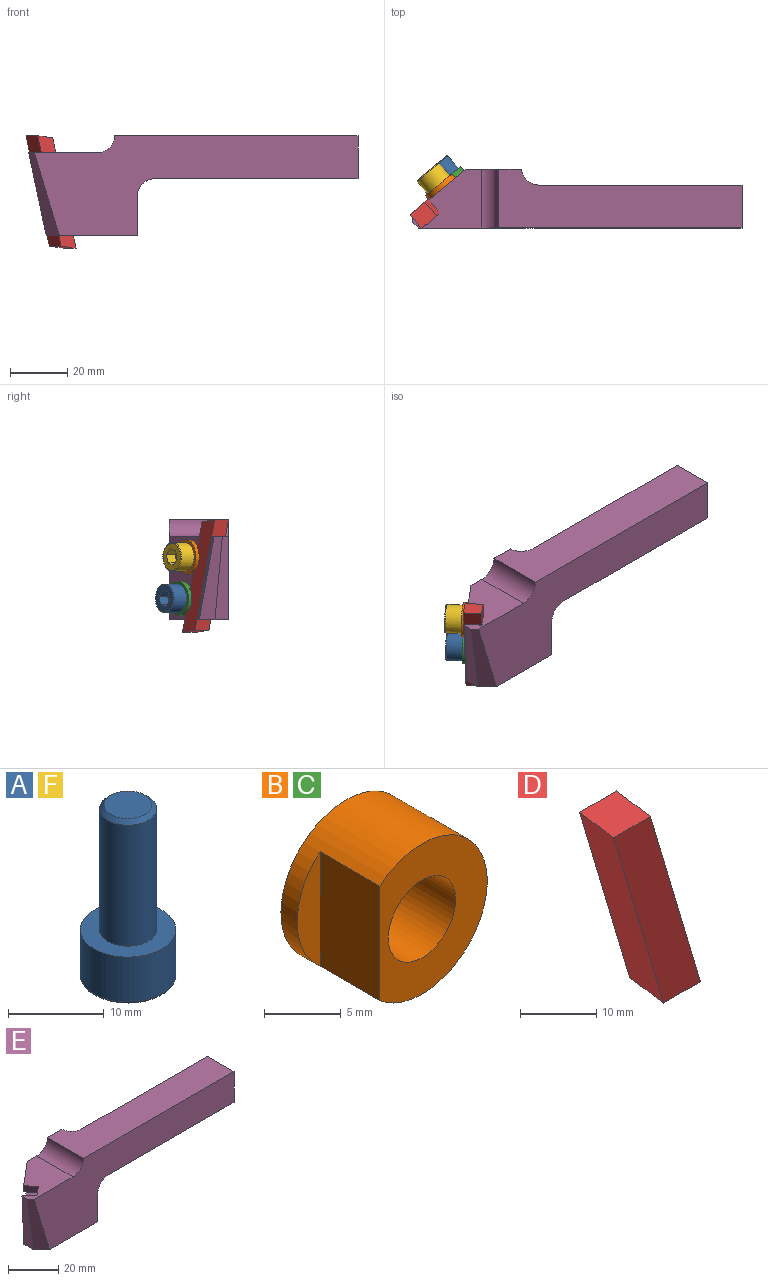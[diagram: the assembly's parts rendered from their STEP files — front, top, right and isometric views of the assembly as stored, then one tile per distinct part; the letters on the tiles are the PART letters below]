
ASSEMBLY  parts=6 mates=10
PART A: 14 faces, bbox 10.8x10.8x22 mm
  f0: plane 10x10mm, normal (0,0,1), area 50.3mm2, adj f1,f3
  f1: cylinder r=5mm len=10mm, axis (0,0,-1), area 180.6mm2, adj f0,f12
  f2: plane 9.5x9.5mm, normal (0,0,-1), area 47.5mm2, adj f5,f6,f7,f8,f9,f10,f12
  f3: cylinder r=3mm len=15.5mm, axis (0,0,-1), area 292.2mm2, adj f0,f13
  f4: plane 5x5mm, normal (0,0,1), area 19.6mm2, adj f13
  f5: plane 4x2.6mm, normal (0.87,-0.5,0), area 12mm2, adj f2,f6,f10,f11
  f6: plane 4x2.6mm, normal (0.87,0.5,0), area 12mm2, adj f2,f5,f7,f11
  f7: plane 4x3mm, normal (0,1,0), area 12mm2, adj f2,f6,f8,f11
  f8: plane 4x2.6mm, normal (-0.87,0.5,0), area 12mm2, adj f2,f7,f9,f11
  f9: plane 4x2.6mm, normal (-0.87,-0.5,0), area 12mm2, adj f2,f8,f10,f11
  f10: plane 4x3mm, normal (0,-1,0), area 12mm2, adj f2,f5,f9,f11
  f11: plane 6x5.2mm, normal (0,0,-1), area 23.4mm2, adj f5,f6,f7,f8,f9,f10
  f12: torus R=4.75mm, axis (0,0,1), area 12.1mm2, adj f1,f2
  f13: cone r=2.5mm half-angle=45deg, axis (0,0,-1), area 12.2mm2, adj f3,f4
PART B: 6 faces, bbox 12x7x12 mm
  f0: plane 12x9.9mm, normal (0,-1,0), area 69.6mm2, adj f1,f2,f4
  f1: cylinder r=3.1mm len=7mm, axis (0,1,0), area 136.3mm2, adj f0,f3
  f2: cylinder r=6mm len=12mm, axis (0,1,0), area 206.9mm2, adj f0,f3,f4,f5
  f3: plane 12x12mm, normal (0,1,0), area 82.9mm2, adj f1,f2
  f4: plane 9.12x5.5mm, normal (-1,0,0), area 50.2mm2, adj f0,f2,f5
  f5: plane 9.12x2.1mm, normal (0,-1,0), area 13.3mm2, adj f2,f4
PART C: same geometry as B
PART D: 6 faces, bbox 21.7x11.8x37.7 mm
  f0: plane 37.68x14.84mm, normal (0.93,-0.06,0.37), area 254mm2, adj f1,f3,f4,f5
  f1: plane 6.84x6.28mm, normal (0,-0.15,0.99), area 43.4mm2, adj f0,f2,f4,f5
  f2: plane 37.68x14.84mm, normal (-0.93,0.06,-0.37), area 254mm2, adj f1,f3,f4,f5
  f3: plane 6.84x6.28mm, normal (0,0.15,-0.99), area 43.4mm2, adj f0,f2,f4,f5
  f4: plane 36.73x21.68mm, normal (0,-0.99,-0.15), area 254mm2, adj f0,f1,f2,f3
  f5: plane 36.73x21.68mm, normal (0,0.99,0.15), area 254mm2, adj f0,f1,f2,f3
PART E: 27 faces, bbox 115x20.5x35 mm
  f0: plane 85x20.5mm, normal (0,0,1), area 1326.7mm2, adj f1,f3,f9,f11,f12,f25
  f1: cylinder r=6mm len=20.5mm, axis (0,0,1), area 151.5mm2, adj f0,f2,f11,f25
  f2: cylinder r=6mm len=20.5mm, axis (0,1,0), area 161.8mm2, adj f1,f9,f11,f24,f26
  f3: plane 15x15mm, normal (1,0,0), area 225mm2, adj f0,f9,f25,f26
  f4: plane 29x12.93mm, normal (-0.64,0.77,0), area 171.5mm2, adj f5,f6,f7,f8,f11,f16,f18,f21
  f5: plane 4.91x4.25mm, normal (-0.74,-0.62,-0.27), area 13.3mm2, adj f4,f8,f17,f21
  f6: plane 5.84x5.56mm, normal (-0.74,-0.62,-0.27), area 35.7mm2, adj f4,f17,f18,f21
  f7: plane 24x20.5mm, normal (0,0,1), area 305.4mm2, adj f4,f9,f10,f11,f12,f13,f14,f15
  f8: plane 31.84x20.5mm, normal (0,0,-1), area 538.1mm2, adj f4,f5,f9,f10,f11,f13,f14,f15
  f9: plane 113x35mm, normal (0,-1,0), area 2136mm2, adj f0,f2,f3,f7,f8,f12,f14,f24
  f10: plane 29x8.03mm, normal (-0.98,0,-0.21), area 123.7mm2, adj f7,f8,f13,f14
  f11: plane 35x19.38mm, normal (0,1,0), area 617.7mm2, adj f0,f1,f2,f4,f7,f8,f12,f24
  f12: cylinder r=6mm len=20.5mm, axis (0,1,0), area 193.2mm2, adj f0,f7,f9,f11
  f13: plane 29x6.82mm, normal (-0.64,0.77,0), area 24.8mm2, adj f7,f8,f10,f15
  f14: plane 29x10.72mm, normal (-0.69,-0.69,-0.21), area 137.4mm2, adj f7,f8,f9,f10
  f15: plane 29x9.96mm, normal (0.74,0.62,0.27), area 177.6mm2, adj f7,f8,f13,f17
  f16: plane 5.19x4.59mm, normal (-0.74,-0.62,-0.27), area 23mm2, adj f4,f7,f17,f18
  f17: plane 29x17.38mm, normal (-0.64,0.77,0), area 353.3mm2, adj f5,f6,f7,f8,f15,f16,f18,f20
  f18: cylinder r=6mm len=12.26mm, axis (-0.64,0.77,0), area 162.9mm2, adj f4,f6,f16,f17
  f19: cone r=0mm half-angle=59deg, axis (-0.64,0.77,0), area 22.9mm2, adj f20
  f20: cylinder r=2.5mm len=9.42mm, axis (-0.64,0.77,0), area 127.2mm2, adj f17,f19
  f21: cylinder r=6mm len=12.26mm, axis (-0.64,0.77,0), area 162.9mm2, adj f4,f5,f6,f17
  f22: cone r=0mm half-angle=59deg, axis (-0.64,0.77,0), area 22.9mm2, adj f23
  f23: cylinder r=2.5mm len=9.42mm, axis (-0.64,0.77,0), area 127.2mm2, adj f17,f22
  f24: plane 20.5x14mm, normal (1,0,0), area 287mm2, adj f2,f8,f9,f11
  f25: plane 71x15mm, normal (0,1,0), area 1065mm2, adj f0,f1,f3,f26
  f26: plane 71x15mm, normal (0,0,-1), area 1065mm2, adj f2,f3,f9,f25
PART F: same geometry as A
PLACE A rot(axis=(0.89,0.19,0.42),102.5deg) t=(-90.86,34.46,28.57)mm
PLACE B rot(axis=(0.13,-0.35,0.93),42.8deg) t=(-60.12,28.45,22.88)mm
PLACE C rot(axis=(0.13,-0.35,0.93),42.8deg) t=(-57.05,31.03,8.43)mm
PLACE D rot(axis=(-0.25,0.07,0.97),41.8deg) t=(-83.81,-1.8,-1.89)mm
PLACE E t=(0,-25,35)mm fixed
PLACE F rot(axis=(0.89,0.19,0.42),102.5deg) t=(-93.93,31.88,43.02)mm
MATE planar E.f15 <-> D.f2  axis (0.74,0.62,0.27) through (-109.37,-19.26,14.5)mm
MATE fastened B.f1 <-> F.f1  axis (-0.64,0.77,0) through (-105.88,-9.94,22)mm
MATE parallel B.f4 <-> D.f0  axis (-0.74,-0.62,-0.27) through (-106.03,-15.61,20.96)mm
MATE cylindrical E.f19 <-> B.f1  axis (-0.64,0.77,0) through (-104.63,-11.44,22)mm
MATE planar C.f5 <-> D.f5  axis (0.64,-0.77,0) through (-105.35,-11.46,6.28)mm
MATE cylindrical C.f1 <-> E.f22  axis (-0.64,0.77,0) through (-102.81,-7.36,7.55)mm
MATE planar E.f17 <-> D.f4  axis (-0.64,0.77,0) through (-102.1,-17.02,14.72)mm
MATE fastened C.f1 <-> A.f1  axis (-0.64,0.77,0) through (-102.81,-7.36,7.55)mm
MATE parallel C.f4 <-> D.f0  axis (-0.74,-0.62,-0.27) through (-102.96,-13.03,6.5)mm
MATE planar B.f5 <-> D.f5  axis (0.64,-0.77,0) through (-108.43,-14.04,20.73)mm
